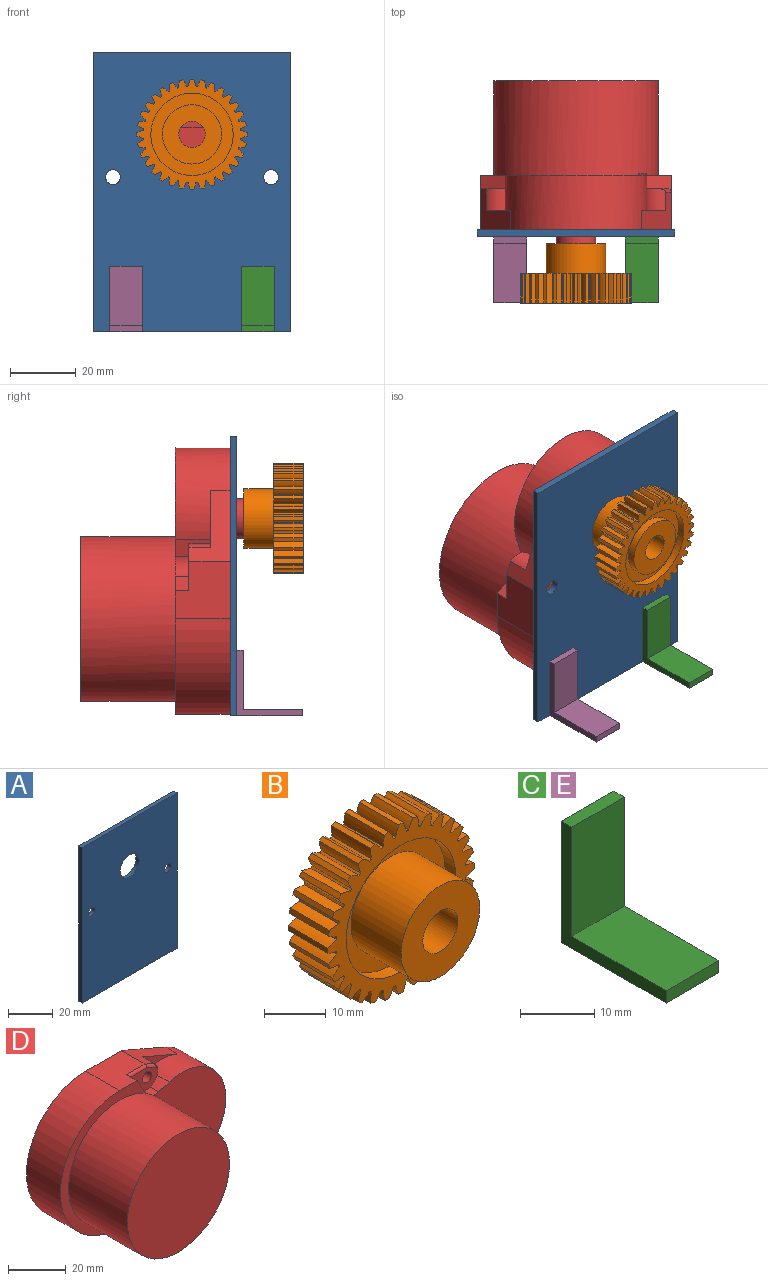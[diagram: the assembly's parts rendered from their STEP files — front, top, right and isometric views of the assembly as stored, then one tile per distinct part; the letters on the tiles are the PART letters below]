
ASSEMBLY  parts=5 mates=4
PART A: 9 faces, bbox 60x2x85 mm
  f0: plane 60x2mm, normal (0,0,1), area 120mm2, adj f1,f6,f7,f8
  f1: plane 85x2mm, normal (-1,0,0), area 170mm2, adj f0,f2,f7,f8
  f2: plane 60x2mm, normal (0,0,-1), area 120mm2, adj f1,f6,f7,f8
  f3: cylinder r=2.25mm len=4.5mm, axis (0,1,0), area 28.3mm2, adj f7,f8
  f4: cylinder r=2.25mm len=4.5mm, axis (0,1,0), area 28.3mm2, adj f7,f8
  f5: cylinder r=6mm len=12mm, axis (0,1,0), area 75.4mm2, adj f7,f8
  f6: plane 85x2mm, normal (1,0,0), area 170mm2, adj f0,f2,f7,f8
  f7: plane 85x60mm, normal (0,-1,0), area 4955.1mm2, adj f0,f1,f2,f3,f4,f5,f6
  f8: plane 85x60mm, normal (0,1,0), area 4955.1mm2, adj f0,f1,f2,f3,f4,f5,f6
PART B: 139 faces, bbox 33.5x18x33.5 mm
  f0: plane 18x18mm, normal (0,1,0), area 204.2mm2, adj f133,f136
  f1: cylinder r=14.75mm len=9mm, axis (0,1,0), area 4.5mm2, adj f32,f37,f38,f86
  f2: cylinder r=14.75mm len=9mm, axis (0,1,0), area 4.5mm2, adj f37,f38,f83,f85
  f3: cylinder r=14.75mm len=9mm, axis (0,1,0), area 4.5mm2, adj f37,f38,f80,f82
  f4: cylinder r=14.75mm len=9mm, axis (0,1,0), area 4.5mm2, adj f37,f38,f77,f79
  f5: cylinder r=14.75mm len=9mm, axis (0,1,0), area 4.5mm2, adj f37,f38,f74,f76
  f6: cylinder r=14.75mm len=9mm, axis (0,1,0), area 4.5mm2, adj f37,f38,f71,f73
  f7: cylinder r=14.75mm len=9mm, axis (0,1,0), area 4.5mm2, adj f37,f38,f68,f70
  f8: cylinder r=14.75mm len=9mm, axis (0,1,0), area 4.5mm2, adj f37,f38,f65,f67
  f9: cylinder r=14.75mm len=9mm, axis (0,1,0), area 4.5mm2, adj f37,f38,f62,f64
  f10: cylinder r=14.75mm len=9mm, axis (0,1,0), area 4.5mm2, adj f37,f38,f59,f61
  f11: cylinder r=14.75mm len=9mm, axis (0,1,0), area 4.5mm2, adj f37,f38,f56,f58
  f12: cylinder r=14.75mm len=9mm, axis (0,1,0), area 4.5mm2, adj f37,f38,f53,f55
  f13: cylinder r=14.75mm len=9mm, axis (0,1,0), area 4.5mm2, adj f37,f38,f50,f52
  f14: cylinder r=14.75mm len=9mm, axis (0,1,0), area 4.5mm2, adj f37,f38,f47,f49
  f15: cylinder r=14.75mm len=9mm, axis (0,1,0), area 4.5mm2, adj f37,f38,f44,f46
  f16: cylinder r=14.75mm len=9mm, axis (0,1,0), area 4.5mm2, adj f37,f38,f41,f43
  f17: cylinder r=14.75mm len=9mm, axis (0,1,0), area 4.5mm2, adj f37,f38,f40,f130
  f18: cylinder r=14.75mm len=9mm, axis (0,1,0), area 4.5mm2, adj f37,f38,f128,f129
  f19: cylinder r=14.75mm len=9mm, axis (0,1,0), area 4.5mm2, adj f37,f38,f125,f127
  f20: cylinder r=14.75mm len=9mm, axis (0,1,0), area 4.5mm2, adj f37,f38,f122,f124
  f21: cylinder r=14.75mm len=9mm, axis (0,1,0), area 4.5mm2, adj f37,f38,f119,f121
  f22: cylinder r=14.75mm len=9mm, axis (0,1,0), area 4.5mm2, adj f37,f38,f116,f118
  f23: cylinder r=14.75mm len=9mm, axis (0,1,0), area 4.5mm2, adj f37,f38,f113,f115
  f24: cylinder r=14.75mm len=9mm, axis (0,1,0), area 4.5mm2, adj f37,f38,f110,f112
  f25: cylinder r=14.75mm len=9mm, axis (0,1,0), area 4.5mm2, adj f37,f38,f107,f109
  f26: cylinder r=14.75mm len=9mm, axis (0,1,0), area 4.5mm2, adj f37,f38,f104,f106
  f27: cylinder r=14.75mm len=9mm, axis (0,1,0), area 4.5mm2, adj f37,f38,f101,f103
  f28: cylinder r=14.75mm len=9mm, axis (0,1,0), area 4.5mm2, adj f37,f38,f98,f100
  f29: cylinder r=14.75mm len=9mm, axis (0,1,0), area 4.5mm2, adj f37,f38,f95,f97
  f30: cylinder r=14.75mm len=9mm, axis (0,1,0), area 4.5mm2, adj f37,f38,f92,f94
  f31: cylinder r=14.75mm len=9mm, axis (0,1,0), area 4.5mm2, adj f37,f38,f88,f91
  f32: cylinder r=7.95mm len=9mm, axis (0,1,0), area 19.5mm2, adj f1,f36,f37,f38
  f33: cylinder r=14.75mm len=9mm, axis (0,1,0), area 4.5mm2, adj f34,f37,f38,f89
  f34: cylinder r=7.95mm len=9mm, axis (0,1,0), area 19.5mm2, adj f33,f36,f37,f38
  f35: cylinder r=12.5mm len=25mm, axis (0,1,0), area 188.5mm2, adj f37,f132
  f36: plane 9x1mm, normal (0,0,1), area 9mm2, adj f32,f34,f37,f38
  f37: plane 33.5x33.5mm, normal (0,-1,0), area 308.3mm2, adj f1,f2,f3,f4,f5,f6,f7,f8
  f38: plane 33.5x33.5mm, normal (0,1,0), area 308.3mm2, adj f1,f2,f3,f4,f5,f6,f7,f8
  f39: plane 9x1mm, normal (0,0,-1), area 9mm2, adj f37,f38,f40,f41
  f40: cylinder r=7.95mm len=9mm, axis (0,1,0), area 19.5mm2, adj f17,f37,f38,f39
  f41: cylinder r=7.95mm len=9mm, axis (0,1,0), area 19.5mm2, adj f16,f37,f38,f39
  f42: plane 9x0.98mm, normal (-0.2,0,-0.98), area 9mm2, adj f37,f38,f43,f44
  f43: cylinder r=7.95mm len=9mm, axis (0,1,0), area 19.5mm2, adj f16,f37,f38,f42
  f44: cylinder r=7.95mm len=9mm, axis (0,1,0), area 19.5mm2, adj f15,f37,f38,f42
  f45: plane 9x0.92mm, normal (-0.38,0,-0.92), area 9mm2, adj f37,f38,f46,f47
  f46: cylinder r=7.95mm len=9mm, axis (0,1,0), area 19.5mm2, adj f15,f37,f38,f45
  f47: cylinder r=7.95mm len=9mm, axis (0,1,0), area 19.5mm2, adj f14,f37,f38,f45
  f48: plane 9x0.83mm, normal (-0.56,0,-0.83), area 9mm2, adj f37,f38,f49,f50
  f49: cylinder r=7.95mm len=9mm, axis (0,1,0), area 19.5mm2, adj f14,f37,f38,f48
  f50: cylinder r=7.95mm len=9mm, axis (0,1,0), area 19.5mm2, adj f13,f37,f38,f48
  f51: plane 9x0.71mm, normal (-0.71,0,-0.71), area 9mm2, adj f37,f38,f52,f53
  f52: cylinder r=7.95mm len=9mm, axis (0,1,0), area 19.5mm2, adj f13,f37,f38,f51
  f53: cylinder r=7.95mm len=9mm, axis (0,1,0), area 19.5mm2, adj f12,f37,f38,f51
  f54: plane 9x0.83mm, normal (-0.83,0,-0.56), area 9mm2, adj f37,f38,f55,f56
  f55: cylinder r=7.95mm len=9mm, axis (0,1,0), area 19.5mm2, adj f12,f37,f38,f54
  f56: cylinder r=7.95mm len=9mm, axis (0,1,0), area 19.5mm2, adj f11,f37,f38,f54
  f57: plane 9x0.92mm, normal (-0.92,0,-0.38), area 9mm2, adj f37,f38,f58,f59
  f58: cylinder r=7.95mm len=9mm, axis (0,1,0), area 19.5mm2, adj f11,f37,f38,f57
  f59: cylinder r=7.95mm len=9mm, axis (0,1,0), area 19.5mm2, adj f10,f37,f38,f57
  f60: plane 9x0.98mm, normal (-0.98,0,-0.2), area 9mm2, adj f37,f38,f61,f62
  f61: cylinder r=7.95mm len=9mm, axis (0,1,0), area 19.5mm2, adj f10,f37,f38,f60
  f62: cylinder r=7.95mm len=9mm, axis (0,1,0), area 19.5mm2, adj f9,f37,f38,f60
  f63: plane 9x1mm, normal (-1,0,0), area 9mm2, adj f37,f38,f64,f65
  f64: cylinder r=7.95mm len=9mm, axis (0,1,0), area 19.5mm2, adj f9,f37,f38,f63
  f65: cylinder r=7.95mm len=9mm, axis (0,1,0), area 19.5mm2, adj f8,f37,f38,f63
  f66: plane 9x0.98mm, normal (-0.98,0,0.2), area 9mm2, adj f37,f38,f67,f68
  f67: cylinder r=7.95mm len=9mm, axis (0,1,0), area 19.5mm2, adj f8,f37,f38,f66
  f68: cylinder r=7.95mm len=9mm, axis (0,1,0), area 19.5mm2, adj f7,f37,f38,f66
  f69: plane 9x0.92mm, normal (-0.92,0,0.38), area 9mm2, adj f37,f38,f70,f71
  f70: cylinder r=7.95mm len=9mm, axis (0,1,0), area 19.5mm2, adj f7,f37,f38,f69
  f71: cylinder r=7.95mm len=9mm, axis (0,1,0), area 19.5mm2, adj f6,f37,f38,f69
  f72: plane 9x0.83mm, normal (-0.83,0,0.56), area 9mm2, adj f37,f38,f73,f74
  f73: cylinder r=7.95mm len=9mm, axis (0,1,0), area 19.5mm2, adj f6,f37,f38,f72
  f74: cylinder r=7.95mm len=9mm, axis (0,1,0), area 19.5mm2, adj f5,f37,f38,f72
  f75: plane 9x0.71mm, normal (-0.71,0,0.71), area 9mm2, adj f37,f38,f76,f77
  f76: cylinder r=7.95mm len=9mm, axis (0,1,0), area 19.5mm2, adj f5,f37,f38,f75
  f77: cylinder r=7.95mm len=9mm, axis (0,1,0), area 19.5mm2, adj f4,f37,f38,f75
  f78: plane 9x0.83mm, normal (-0.56,0,0.83), area 9mm2, adj f37,f38,f79,f80
  f79: cylinder r=7.95mm len=9mm, axis (0,1,0), area 19.5mm2, adj f4,f37,f38,f78
  f80: cylinder r=7.95mm len=9mm, axis (0,1,0), area 19.5mm2, adj f3,f37,f38,f78
  f81: plane 9x0.92mm, normal (-0.38,0,0.92), area 9mm2, adj f37,f38,f82,f83
  f82: cylinder r=7.95mm len=9mm, axis (0,1,0), area 19.5mm2, adj f3,f37,f38,f81
  f83: cylinder r=7.95mm len=9mm, axis (0,1,0), area 19.5mm2, adj f2,f37,f38,f81
  f84: plane 9x0.98mm, normal (-0.2,0,0.98), area 9mm2, adj f37,f38,f85,f86
  f85: cylinder r=7.95mm len=9mm, axis (0,1,0), area 19.5mm2, adj f2,f37,f38,f84
  f86: cylinder r=7.95mm len=9mm, axis (0,1,0), area 19.5mm2, adj f1,f37,f38,f84
  f87: plane 9x0.98mm, normal (0.2,0,0.98), area 9mm2, adj f37,f38,f88,f89
  f88: cylinder r=7.95mm len=9mm, axis (0,1,0), area 19.5mm2, adj f31,f37,f38,f87
  f89: cylinder r=7.95mm len=9mm, axis (0,1,0), area 19.5mm2, adj f33,f37,f38,f87
  f90: plane 9x0.92mm, normal (0.38,0,0.92), area 9mm2, adj f37,f38,f91,f92
  f91: cylinder r=7.95mm len=9mm, axis (0,1,0), area 19.5mm2, adj f31,f37,f38,f90
  f92: cylinder r=7.95mm len=9mm, axis (0,1,0), area 19.5mm2, adj f30,f37,f38,f90
  f93: plane 9x0.83mm, normal (0.56,0,0.83), area 9mm2, adj f37,f38,f94,f95
  f94: cylinder r=7.95mm len=9mm, axis (0,1,0), area 19.5mm2, adj f30,f37,f38,f93
  f95: cylinder r=7.95mm len=9mm, axis (0,1,0), area 19.5mm2, adj f29,f37,f38,f93
  f96: plane 9x0.71mm, normal (0.71,0,0.71), area 9mm2, adj f37,f38,f97,f98
  f97: cylinder r=7.95mm len=9mm, axis (0,1,0), area 19.5mm2, adj f29,f37,f38,f96
  f98: cylinder r=7.95mm len=9mm, axis (0,1,0), area 19.5mm2, adj f28,f37,f38,f96
  f99: plane 9x0.83mm, normal (0.83,0,0.56), area 9mm2, adj f37,f38,f100,f101
  f100: cylinder r=7.95mm len=9mm, axis (0,1,0), area 19.5mm2, adj f28,f37,f38,f99
  f101: cylinder r=7.95mm len=9mm, axis (0,1,0), area 19.5mm2, adj f27,f37,f38,f99
  f102: plane 9x0.92mm, normal (0.92,0,0.38), area 9mm2, adj f37,f38,f103,f104
  f103: cylinder r=7.95mm len=9mm, axis (0,1,0), area 19.5mm2, adj f27,f37,f38,f102
  f104: cylinder r=7.95mm len=9mm, axis (0,1,0), area 19.5mm2, adj f26,f37,f38,f102
  f105: plane 9x0.98mm, normal (0.98,0,0.2), area 9mm2, adj f37,f38,f106,f107
  f106: cylinder r=7.95mm len=9mm, axis (0,1,0), area 19.5mm2, adj f26,f37,f38,f105
  f107: cylinder r=7.95mm len=9mm, axis (0,1,0), area 19.5mm2, adj f25,f37,f38,f105
  f108: plane 9x1mm, normal (1,0,0), area 9mm2, adj f37,f38,f109,f110
  f109: cylinder r=7.95mm len=9mm, axis (0,1,0), area 19.5mm2, adj f25,f37,f38,f108
  f110: cylinder r=7.95mm len=9mm, axis (0,1,0), area 19.5mm2, adj f24,f37,f38,f108
  f111: plane 9x0.98mm, normal (0.98,0,-0.2), area 9mm2, adj f37,f38,f112,f113
  f112: cylinder r=7.95mm len=9mm, axis (0,1,0), area 19.5mm2, adj f24,f37,f38,f111
  f113: cylinder r=7.95mm len=9mm, axis (0,1,0), area 19.5mm2, adj f23,f37,f38,f111
  f114: plane 9x0.92mm, normal (0.92,0,-0.38), area 9mm2, adj f37,f38,f115,f116
  f115: cylinder r=7.95mm len=9mm, axis (0,1,0), area 19.5mm2, adj f23,f37,f38,f114
  f116: cylinder r=7.95mm len=9mm, axis (0,1,0), area 19.5mm2, adj f22,f37,f38,f114
  f117: plane 9x0.83mm, normal (0.83,0,-0.56), area 9mm2, adj f37,f38,f118,f119
  f118: cylinder r=7.95mm len=9mm, axis (0,1,0), area 19.5mm2, adj f22,f37,f38,f117
  f119: cylinder r=7.95mm len=9mm, axis (0,1,0), area 19.5mm2, adj f21,f37,f38,f117
  f120: plane 9x0.71mm, normal (0.71,0,-0.71), area 9mm2, adj f37,f38,f121,f122
  f121: cylinder r=7.95mm len=9mm, axis (0,1,0), area 19.5mm2, adj f21,f37,f38,f120
  f122: cylinder r=7.95mm len=9mm, axis (0,1,0), area 19.5mm2, adj f20,f37,f38,f120
  f123: plane 9x0.83mm, normal (0.56,0,-0.83), area 9mm2, adj f37,f38,f124,f125
  f124: cylinder r=7.95mm len=9mm, axis (0,1,0), area 19.5mm2, adj f20,f37,f38,f123
  f125: cylinder r=7.95mm len=9mm, axis (0,1,0), area 19.5mm2, adj f19,f37,f38,f123
  f126: plane 9x0.92mm, normal (0.38,0,-0.92), area 9mm2, adj f37,f38,f127,f128
  f127: cylinder r=7.95mm len=9mm, axis (0,1,0), area 19.5mm2, adj f19,f37,f38,f126
  f128: cylinder r=7.95mm len=9mm, axis (0,1,0), area 19.5mm2, adj f18,f37,f38,f126
  f129: cylinder r=7.95mm len=9mm, axis (0,1,0), area 19.5mm2, adj f18,f37,f38,f131
  f130: cylinder r=7.95mm len=9mm, axis (0,1,0), area 19.5mm2, adj f17,f37,f38,f131
  f131: plane 9x0.98mm, normal (0.2,0,-0.98), area 9mm2, adj f37,f38,f129,f130
  f132: plane 25x25mm, normal (0,-1,0), area 236.4mm2, adj f35,f134
  f133: cylinder r=4mm len=18mm, axis (0,1,0), area 452.4mm2, adj f0,f135
  f134: cylinder r=9mm len=18mm, axis (0,1,0), area 644.7mm2, adj f132,f135
  f135: plane 18x18mm, normal (0,-1,0), area 204.2mm2, adj f133,f134
  f136: cylinder r=9mm len=18mm, axis (0,1,0), area 135.7mm2, adj f0,f138
  f137: cylinder r=12.5mm len=25mm, axis (0,1,0), area 188.5mm2, adj f38,f138
  f138: plane 25x25mm, normal (0,1,0), area 236.4mm2, adj f136,f137
PART C: 8 faces, bbox 10x20x20 mm
  f0: plane 18x10mm, normal (0,-1,0), area 180mm2, adj f1,f2,f3,f6
  f1: plane 20x20mm, normal (1,0,0), area 76mm2, adj f0,f2,f4,f5,f6,f7
  f2: plane 10x2mm, normal (0,0,1), area 20mm2, adj f0,f1,f3,f5
  f3: plane 20x20mm, normal (-1,0,0), area 76mm2, adj f0,f2,f4,f5,f6,f7
  f4: plane 20x10mm, normal (0,0,-1), area 200mm2, adj f1,f3,f5,f7
  f5: plane 20x10mm, normal (0,1,0), area 200mm2, adj f1,f2,f3,f4
  f6: plane 18x10mm, normal (0,0,1), area 180mm2, adj f0,f1,f3,f7
  f7: plane 10x2mm, normal (0,-1,0), area 20mm2, adj f1,f3,f4,f6
PART D: 48 faces, bbox 81x61.6x58 mm
  f0: plane 43x35.6mm, normal (0,-1,0), area 1071.3mm2, adj f29,f32,f33,f35,f36,f42
  f1: plane 14.25x10.25mm, normal (0,-1,0), area 85.3mm2, adj f6,f7,f28,f31,f33,f39
  f2: plane 21.5x11.5mm, normal (0.4,0,0.92), area 165.3mm2, adj f4,f29,f30,f37,f38,f46
  f3: plane 13.67x9.25mm, normal (0,-1,0), area 71.6mm2, adj f5,f34,f35,f37,f45,f46
  f4: plane 17.5x16.6mm, normal (0,0,1), area 244.6mm2, adj f2,f8,f27,f30,f34,f45
  f5: cylinder r=2.25mm len=11.5mm, axis (0,1,0), area 162.6mm2, adj f3,f26
  f6: cylinder r=2.25mm len=11.5mm, axis (0,1,0), area 162.6mm2, adj f1,f26
  f7: plane 21.5x12.5mm, normal (0.4,0,-0.92), area 169.8mm2, adj f1,f28,f29,f30,f39,f40
  f8: plane 58x41.95mm, normal (0,-1,0), area 439.2mm2, adj f4,f27,f28,f31,f34,f42
  f9: plane 8x6mm, normal (0,1,0), area 40.4mm2, adj f10,f14
  f10: cylinder r=4mm len=12mm, axis (0,-1,0), area 234.6mm2, adj f9,f13,f14,f15
  f11: plane 71x48mm, normal (0,1,0), area 2492.1mm2, adj f12,f16,f17,f18,f24
  f12: cylinder r=6mm len=12mm, axis (0,-1,0), area 158.3mm2, adj f11,f13
  f13: plane 12x12mm, normal (0,1,0), area 62.8mm2, adj f10,f12
  f14: plane 8x6.93mm, normal (1,0,0), area 55.4mm2, adj f9,f10,f15
  f15: plane 6.93x2mm, normal (0,1,0), area 9.8mm2, adj f10,f14
  f16: plane 28.66x7.27mm, normal (0.25,0,0.97), area 29.6mm2, adj f11,f17,f24,f26
  f17: cylinder r=16.5mm len=31.99mm, axis (0,1,0), area 43.6mm2, adj f11,f16,f18,f26
  f18: plane 28.66x7.27mm, normal (0.25,0,-0.97), area 29.6mm2, adj f11,f17,f24,f26
  f19: plane 21.17x9.2mm, normal (-0.4,0,0.92), area 23.1mm2, adj f20,f25,f26,f30
  f20: cylinder r=20.5mm len=37.6mm, axis (0,1,0), area 47.6mm2, adj f19,f21,f26,f30
  f21: plane 21.17x9.2mm, normal (-0.4,0,-0.92), area 23.1mm2, adj f20,f22,f26,f30
  f22: plane 17.5x1mm, normal (0,0,-1), area 17.5mm2, adj f21,f23,f26,f30
  f23: cylinder r=28mm len=56mm, axis (0,1,0), area 88mm2, adj f22,f25,f26,f30
  f24: cylinder r=24mm len=48mm, axis (0,1,0), area 87.3mm2, adj f11,f16,f18,f26
  f25: plane 17.5x1mm, normal (0,0,1), area 17.5mm2, adj f19,f23,f26,f30
  f26: plane 79x56mm, normal (0,1,0), area 899.5mm2, adj f5,f6,f16,f17,f18,f19,f20,f21
  f27: cylinder r=29mm len=58mm, axis (0,1,0), area 1512.4mm2, adj f4,f8,f28,f30
  f28: plane 17.5x16.6mm, normal (0,0,-1), area 253.6mm2, adj f1,f7,f8,f27,f30,f31
  f29: cylinder r=21.5mm len=43mm, axis (0,1,0), area 1151.5mm2, adj f0,f2,f7,f30,f32,f36,f38,f40
  f30: plane 81x58mm, normal (0,1,0), area 217.9mm2, adj f2,f4,f7,f19,f20,f21,f22,f23
  f31: plane 7.65x4.47mm, normal (0.86,0,-0.5), area 36.3mm2, adj f1,f8,f28,f33,f41
  f32: plane 10.6x5.19mm, normal (-0.29,0,-0.96), area 57.5mm2, adj f0,f29,f33,f39,f40
  f33: cylinder r=5.25mm len=6.07mm, axis (0,-1,0), area 28.8mm2, adj f0,f1,f31,f32,f41
  f34: plane 7.66x5.62mm, normal (0.86,0,0.5), area 36.6mm2, adj f3,f4,f8,f35,f42,f45,f47
  f35: cylinder r=5.25mm len=6.07mm, axis (0,-1,0), area 29mm2, adj f0,f3,f34,f36,f42,f44,f47
  f36: plane 10.6x5.19mm, normal (-0.29,0,0.96), area 57.5mm2, adj f0,f29,f35,f37,f38
  f37: cylinder r=5.25mm len=8.23mm, axis (0,-1,0), area 65.6mm2, adj f2,f3,f36,f38,f46
  f38: plane 19.97x8.23mm, normal (0,-1,0), area 40.6mm2, adj f2,f29,f36,f37
  f39: cylinder r=5.25mm len=8.23mm, axis (0,-1,0), area 66mm2, adj f1,f7,f32,f40
  f40: plane 19.97x8.23mm, normal (0,-1,0), area 40.6mm2, adj f7,f29,f32,f39
  f41: plane 3.46x2.52mm, normal (0,1,0), area 1.6mm2, adj f31,f33,f42
  f42: cylinder r=25mm len=50mm, axis (0,1,0), area 4513.9mm2, adj f0,f8,f34,f35,f41,f43,f47
  f43: plane 50x50mm, normal (0,-1,0), area 1963.5mm2, adj f42
  f44: plane 1.03x0.75mm, normal (0,1,0), area 0mm2, adj f35,f47
  f45: cylinder r=1mm len=9mm, axis (1,0,0), area 13.6mm2, adj f3,f4,f34,f46
  f46: cylinder r=1mm len=5.73mm, axis (0.92,0,-0.4), area 7.8mm2, adj f2,f3,f37,f45
  f47: torus R=24.5mm, axis (0,-1,0), area 2.7mm2, adj f34,f35,f42,f44
PART E: same geometry as C
PLACE A t=(-17.13,-43.09,4.55)mm
PLACE B rot(axis=(0,0,-1),180deg) t=(-13.1,-65.29,14.92)mm
PLACE C t=(18.11,-45.09,-6.06)mm
PLACE D rot(axis=(-0.71,0,-0.71),180deg) t=(-13.1,-43.09,-15.58)mm
PLACE E t=(-21.89,-45.09,-6.06)mm
MATE fastened E.f5 <-> A.f7  axis (0,1,0) through (-38.1,-45.09,-25.08)mm
MATE fastened B.f133 <-> D.f10  axis (0,-1,0) through (-13.1,-47.29,14.92)mm
MATE fastened D.f12 <-> A.f5  axis (0,1,0) through (-13.1,-43.09,14.92)mm
MATE fastened C.f5 <-> A.f7  axis (0,1,0) through (11.9,-45.09,-25.08)mm
